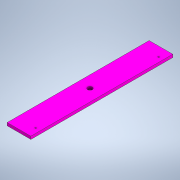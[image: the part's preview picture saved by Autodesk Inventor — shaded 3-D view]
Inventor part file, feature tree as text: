
AUTODESK INVENTOR PART (.ipt)
format: ipt  version: 2022 (Build 260153000, 153)  size: 112,128 bytes
history: native  units: mm
features: extrude x1, sketch x1
ambient origin geometry x8: Origin, YZ Plane, XZ Plane, XY Plane, X Axis, Y Axis, Z Axis, Center Point
bodies: Body1 (feature_tree)
feature tree (2):
  extrude  "Extrusion2"  Depth=50.0mm
  sketch  "Sketch1"  dims[d0=10.0mm d6=50.0mm d7=300.0mm d15=3.0mm d16=10.0mm d17=3.0mm d18=6.0mm d19=0.0mm d20=20.0mm d21=20.0mm]
